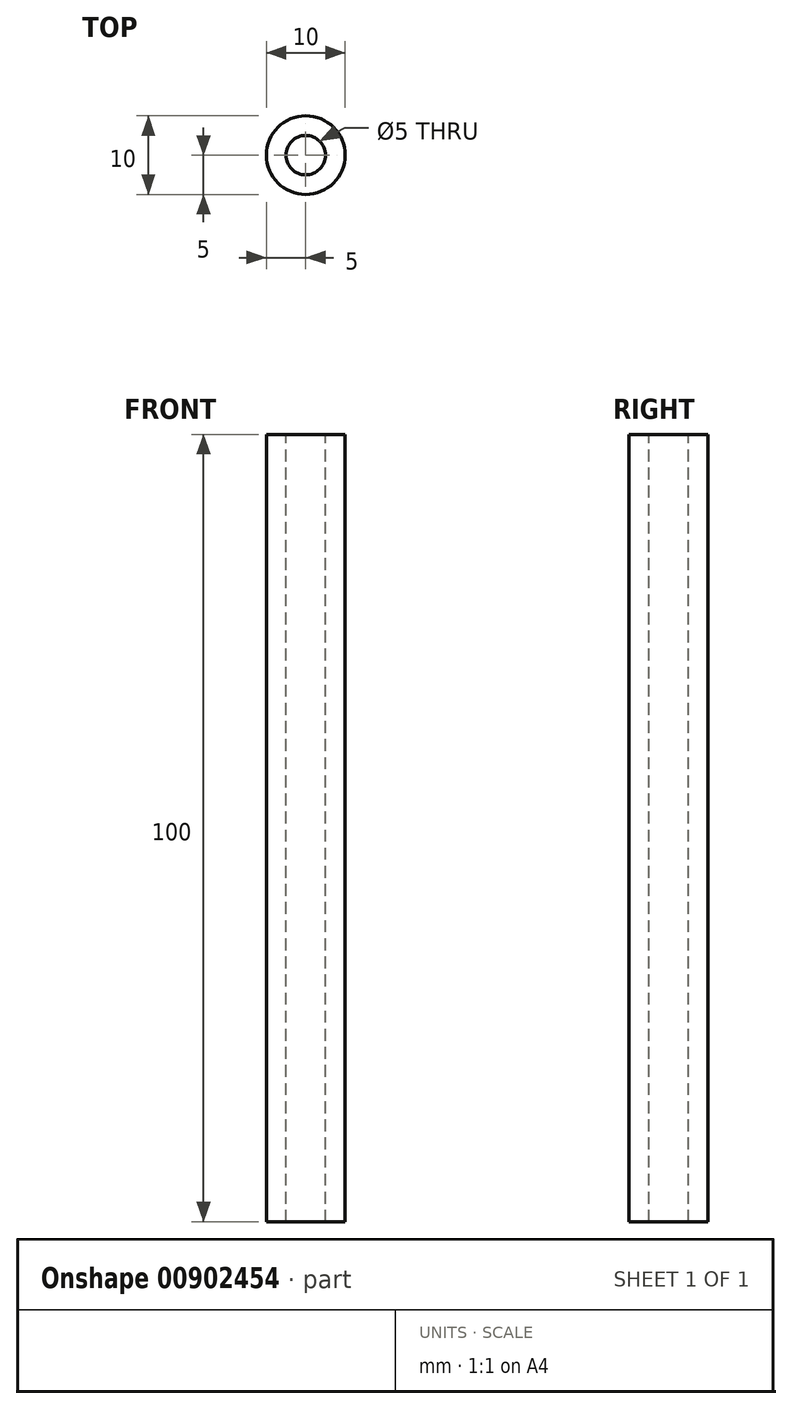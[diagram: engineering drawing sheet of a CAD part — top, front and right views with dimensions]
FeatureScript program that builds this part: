
annotation { "Feature Type Name" : "Feature", "Feature Type Description" : "" }
export const myFeature = defineFeature(function(context is Context, id is Id, definition is map)
    precondition{}
    {
        {
            var Q0;
            Q0=qCreatedBy(makeId("Top.planeOp"),FACE);
            var sketch = newSketch(context, id + "F0", { "sketchPlane" : qUnion([Q0])});
            skCircle(sketch, "E0", {"center": v(0, 0) * mm, "radius": 5 * mm});
            skSolve(sketch);
        }
        {
            var Q0;
            Q0 = qSketchRegion(id + "F0", true);
            extrude(context, id + "F1", {"entities" : qUnion([Q0]), "depth" : 100 * mm, "offsetDistance" : 25 * mm});
        }
        {
            var Q0;
            Q0=makeQuery(id+"F1.opExtrude","CAP_FACE",FACE,{"disambiguationData":[OSD([sQuery(id+"F0.wireOp",EDGE,"E0")])],"isStart":false});
            var sketch = newSketch(context, id + "F2", { "sketchPlane" : qUnion([Q0])});
            skCircle(sketch, "E1", {"center": v(0, 0) * mm, "radius": 2.5 * mm});
            skSolve(sketch);
        }
        {
            var Q0;
            Q0=makeQuery(id+"F2.imprint","IMPRINT",FACE,{"disambiguationData":[TD([[makeQuery(id+"F2.imprint","IMPRINT",EDGE,{"derivedFrom":sQuery(id+"F2.wireOp",EDGE,"E1")}),1.0]])]});
            var Q1;
            Q1=makeQuery(id+"F1.opExtrude","CAP_FACE",FACE,{"disambiguationData":[OSD([sQuery(id+"F0.wireOp",EDGE,"E0")])],"isStart":true});
            extrude(context, id + "F3", {"entities" : qUnion([Q0]), "operationType" : NewBodyOperationType.REMOVE, "endBound" : BoundingType.UP_TO_SURFACE, "oppositeDirection" : true, "depth" : 25 * mm, "endBoundEntityFace" : qUnion([Q1]), "offsetDistance" : 25 * mm});
        }
    });
